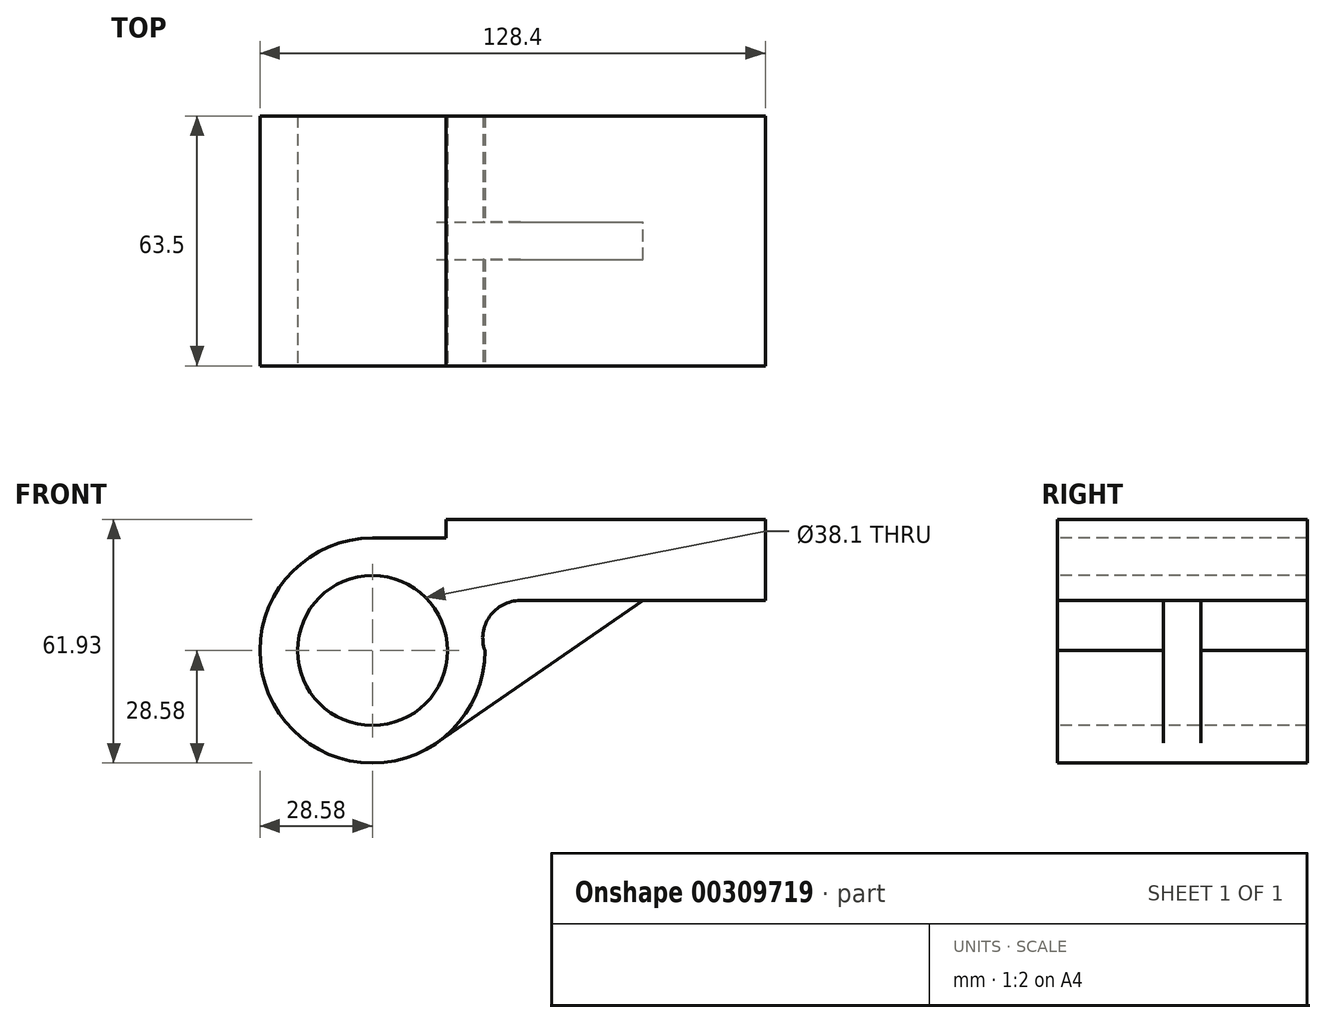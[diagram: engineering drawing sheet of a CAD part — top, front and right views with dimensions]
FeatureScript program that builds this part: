
annotation { "Feature Type Name" : "Feature", "Feature Type Description" : "" }
export const myFeature = defineFeature(function(context is Context, id is Id, definition is map)
    precondition{}
    {
        {
            var Q0;
            Q0=qCreatedBy(makeId("Front.planeOp"),FACE);
            var sketch = newSketch(context, id + "F0", { "sketchPlane" : qUnion([Q0])});
            skCircle(sketch, "E0", {"center": v(0, 0) * mm, "radius": 19.05 * mm});
            skArc(sketch, "E1", {"start": v(0, 28.58) * mm, "mid": v(-20.2, -20.2) * mm, "end": v(28.58, 0) * mm});
            skLineSegment(sketch, "E2", {"start": v(0, 28.58) * mm, "end": v(37.56, 28.58) * mm});
            skLineSegment(sketch, "E3", {"start": v(18.69, 28.58) * mm, "end": v(18.69, 33.35) * mm});
            skLineSegment(sketch, "E4", {"start": v(18.69, 33.35) * mm, "end": v(99.82, 33.35) * mm});
            skLineSegment(sketch, "E5", {"start": v(37.56, 12.7) * mm, "end": v(99.82, 12.7) * mm});
            skLineSegment(sketch, "E6", {"start": v(99.82, 33.35) * mm, "end": v(99.82, 12.7) * mm});
            skLineSegment(sketch, "E7", {"start": v(16.24, -23.51) * mm, "end": v(68.69, 12.7) * mm});
            skArc(sketch, "E8", {"start": v(37.56, 12.7) * mm, "mid": v(29.78, 8.67) * mm, "end": v(28.58, 0) * mm});
            skSolve(sketch);
        }
        {
            var Q0;
            Q0=makeQuery(id+"F0.imprint","IMPRINT",FACE,{"disambiguationData":[TD([[makeQuery(id+"F0.imprint","IMPRINT",EDGE,{"derivedFrom":sQuery(id+"F0.wireOp",EDGE,"E0")}),-1.0]])]});
            extrude(context, id + "F1", {"entities" : qUnion([Q0]), "endBound" : BoundingType.SYMMETRIC, "oppositeDirection" : true, "depth" : 63.5 * mm});
        }
        {
            var Q0;
            {var subQ2=sQuery(id+"F0.wireOp",EDGE,"E7");Q0=makeQuery(id+"F0.imprint","IMPRINT",FACE,{"disambiguationData":[TD([[makeQuery(id+"F0.imprint","IMPRINT",EDGE,{"derivedFrom":subQ2}),1.0]])]});}
            extrude(context, id + "F2", {"entities" : qUnion([Q0]), "operationType" : NewBodyOperationType.ADD, "endBound" : BoundingType.SYMMETRIC, "depth" : 9.52 * mm});
        }
    });
